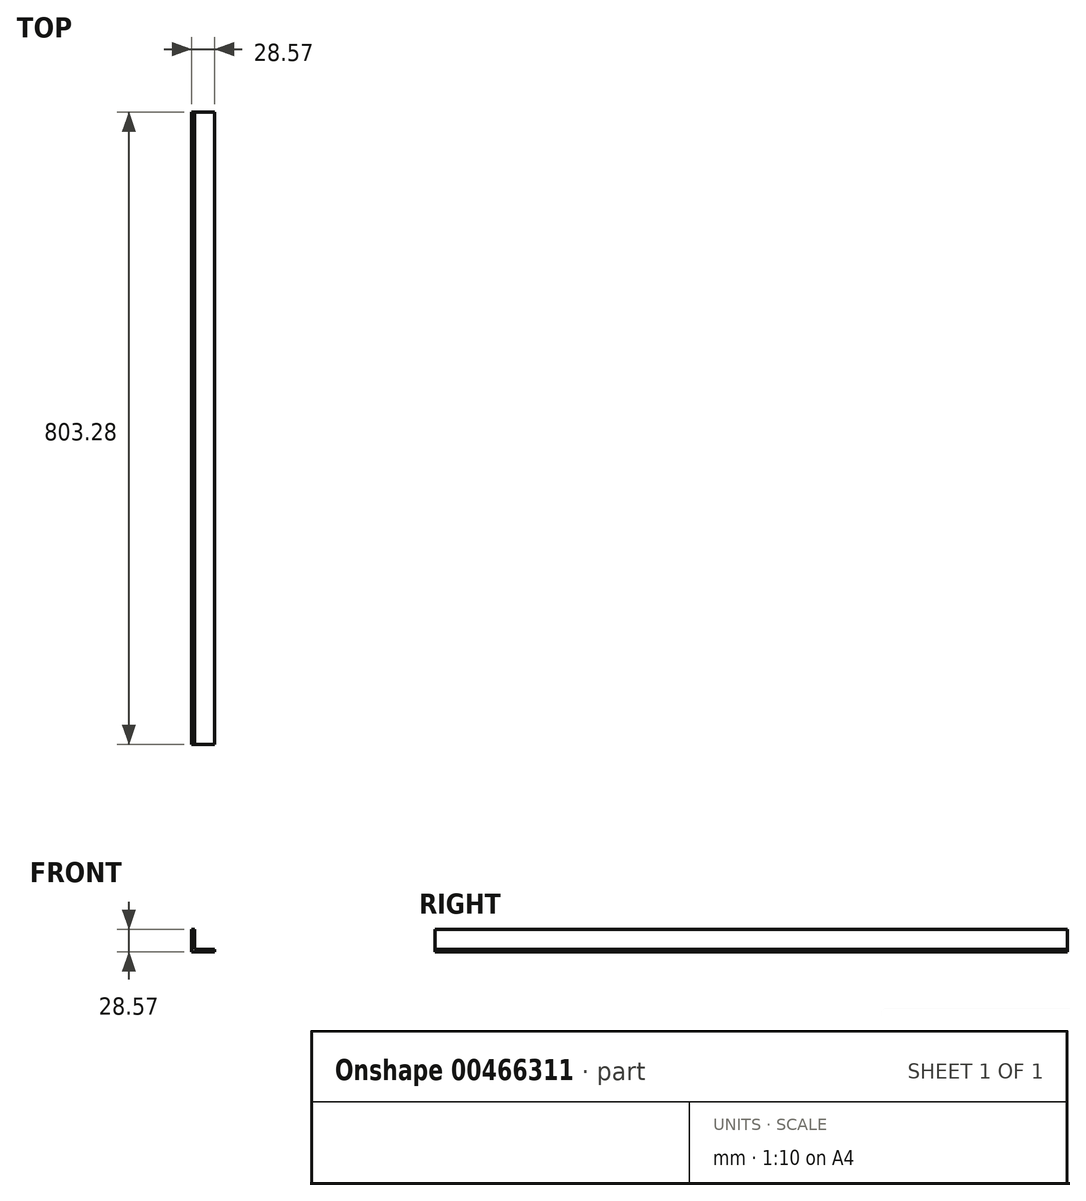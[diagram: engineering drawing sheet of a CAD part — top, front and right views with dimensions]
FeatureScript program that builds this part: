
annotation { "Feature Type Name" : "Feature", "Feature Type Description" : "" }
export const myFeature = defineFeature(function(context is Context, id is Id, definition is map)
    precondition{}
    {
        {
            var Q0;
            Q0=qCreatedBy(makeId("Front.planeOp"),FACE);
            var sketch = newSketch(context, id + "F0", { "sketchPlane" : qUnion([Q0])});
            skLineSegment(sketch, "E0", {"start": v(-25.4, -17.46) * mm, "end": v(0, -17.46) * mm});
            skLineSegment(sketch, "E1", {"start": v(-25.4, -17.46) * mm, "end": v(-25.4, 7.94) * mm});
            skLineSegment(sketch, "E2", {"start": v(-25.4, 7.94) * mm, "end": v(-28.58, 7.94) * mm});
            skLineSegment(sketch, "E3", {"start": v(-28.57, 7.94) * mm, "end": v(-28.57, -20.63) * mm});
            skLineSegment(sketch, "E4", {"start": v(0, -17.46) * mm, "end": v(0, -20.63) * mm});
            skLineSegment(sketch, "E5", {"start": v(0, -20.63) * mm, "end": v(-28.58, -20.63) * mm});
            skSolve(sketch);
        }
        {
            var Q0;
            Q0 = qSketchRegion(id + "F0", true);
            extrude(context, id + "F1", {"entities" : qUnion([Q0]), "depth" : 25.4 * mm});
        }
        {
            var Q0;
            Q0=makeQuery(id+"F1.opExtrude","CAP_FACE",FACE,{"disambiguationData":[OSD([sQuery(id+"F0.wireOp",EDGE,"E0"),sQuery(id+"F0.wireOp",EDGE,"E1"),sQuery(id+"F0.wireOp",EDGE,"E2"),sQuery(id+"F0.wireOp",EDGE,"E3"),sQuery(id+"F0.wireOp",EDGE,"E4"),sQuery(id+"F0.wireOp",EDGE,"E5")])],"isStart":true});
            extrude(context, id + "F2", {"entities" : qUnion([Q0]), "operationType" : NewBodyOperationType.ADD, "depth" : 777.88 * mm});
        }
    });
